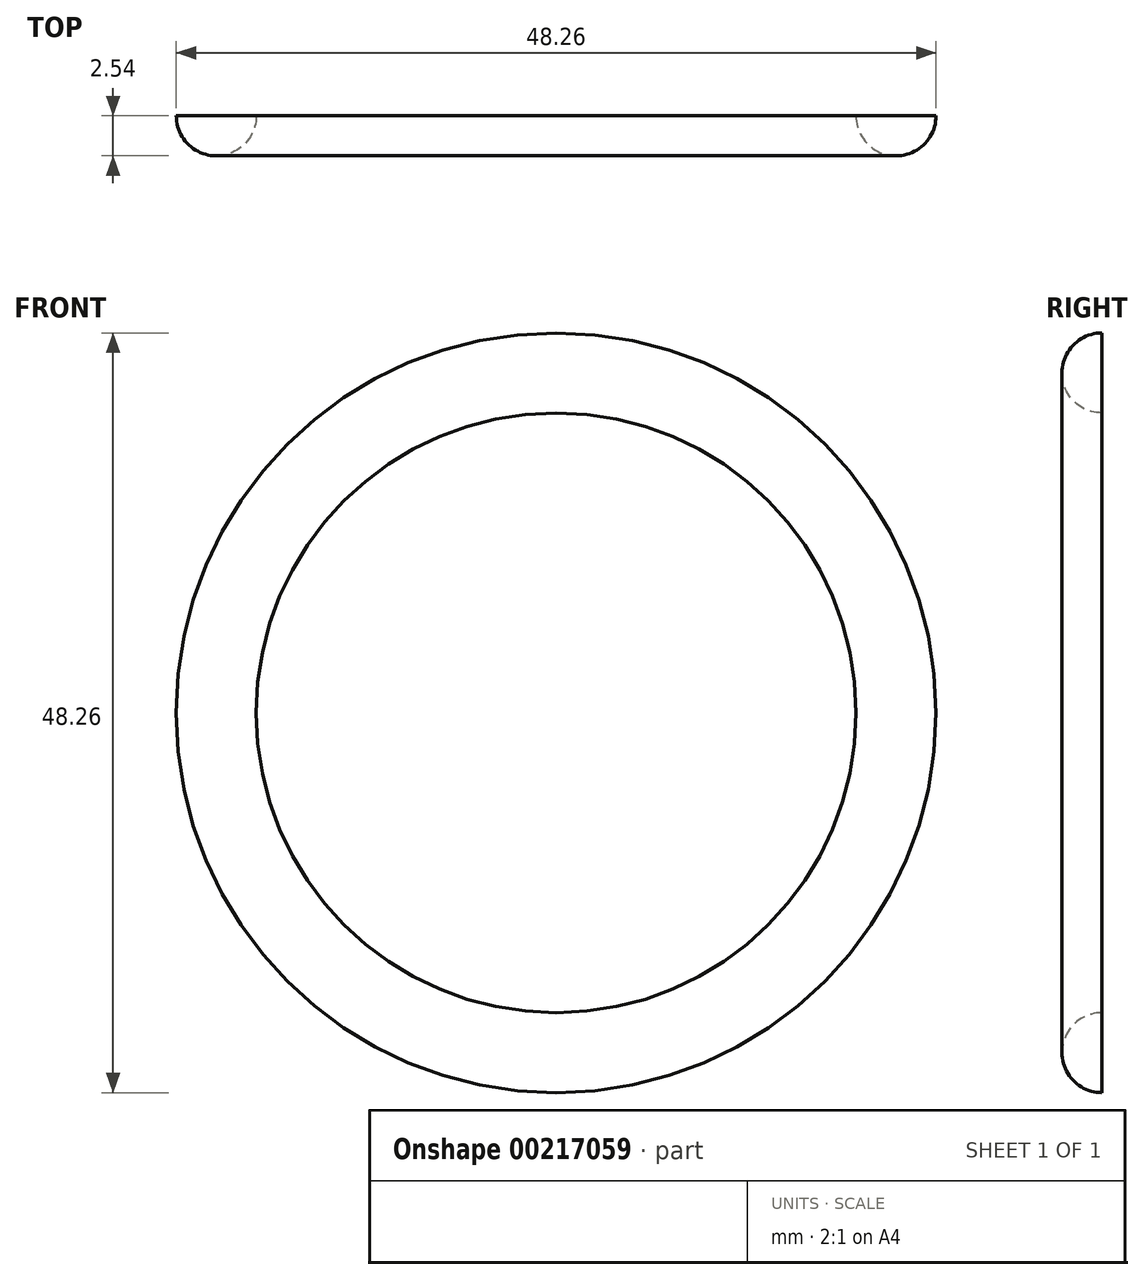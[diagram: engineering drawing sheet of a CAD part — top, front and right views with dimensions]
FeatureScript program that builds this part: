
annotation { "Feature Type Name" : "Feature", "Feature Type Description" : "" }
export const myFeature = defineFeature(function(context is Context, id is Id, definition is map)
    precondition{}
    {
        {
            var Q0;
            Q0=qCreatedBy(makeId("Front.planeOp"),FACE);
            var sketch = newSketch(context, id + "F0", { "sketchPlane" : qUnion([Q0])});
            skCircle(sketch, "E0", {"center": v(0, 0) * mm, "radius": 19.05 * mm});
            skSolve(sketch);
        }
        {
            var Q0;
            Q0=qCreatedBy(makeId("Right.planeOp"),FACE);
            var sketch = newSketch(context, id + "F1", { "sketchPlane" : qUnion([Q0])});
            skArc(sketch, "E1", {"start": v(0, 24.13) * mm, "mid": v(-2.54, 21.59) * mm, "end": v(0, 19.05) * mm});
            skLineSegment(sketch, "E2", {"start": v(0, 24.13) * mm, "end": v(0, 19.05) * mm});
            skSolve(sketch);
        }
        {
            var Q0;
            Q0 = qSketchRegion(id + "F1", true);
            var Q1;
            Q1=sQuery(id+"F0.wireOp",EDGE,"E0");
            revolve(context, id + "F2", {"entities" : qUnion([Q0]), "axis" : qUnion([Q1]), "revolveType" : RevolveType.FULL});
        }
    });
